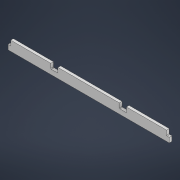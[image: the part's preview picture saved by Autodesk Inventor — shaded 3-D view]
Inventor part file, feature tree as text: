
AUTODESK INVENTOR PART (.ipt)
format: ipt  version: 2021 (Build 250183000, 183)  size: 138,240 bytes
history: native  units: mm
features: plane x3, extrude x2, sketch x2, fillet x1
ambient origin geometry x8: Origin, YZ Plane, XZ Plane, XY Plane, X Axis, Y Axis, Z Axis, Center Point
bodies: Solid1 (feature_tree)
feature tree (8):
  extrude  "Extrusion1"  Depth=55.0mm
  plane  "Work Plane1"
  extrude  "Extrusion2"  Depth=15.0mm
  plane  "Work Plane2"
  plane  "Work Plane3"
  fillet  "Fillet1"  Radius=27.5mm
  sketch  "Sketch1"  dims[d0=910.0mm d1=55.0mm]
  sketch  "Sketch3"  dims[d2=15.0mm d3=0.0mm d12=15.0mm d13=27.5mm d14=226.667mm d15=40.0mm d16=0.0mm d17=0.0mm d18=3.0mm]
